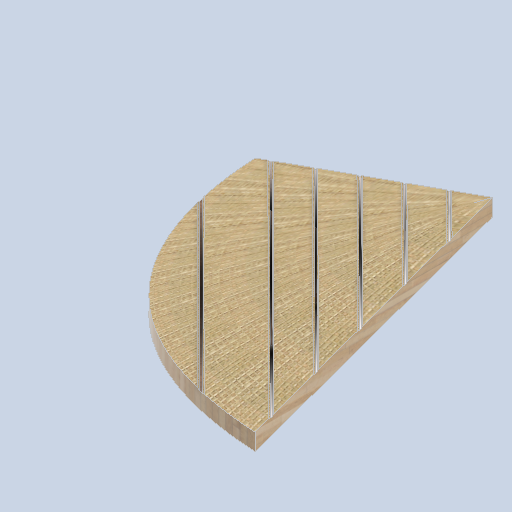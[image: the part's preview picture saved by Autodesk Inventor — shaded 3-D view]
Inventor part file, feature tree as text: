
AUTODESK INVENTOR PART (.ipt)
format: ipt  version: 2024.2 (Build 282272000, 272)  size: 927,744 bytes
history: native  units: in
note: dims shown in document units (in); Inventor stores cm internally (conversion verified against a paired STEP export)
features: sketch x19, plane x6, other x3
ambient origin geometry x8: Origin, YZ Plane, XZ Plane, XY Plane, X Axis, Y Axis, Z Axis, Center Point
bodies: Solid1 (feature_tree)
feature tree (28):
  other  "side_curve_corner_panel_MIR.ipt"
  other  "Solid1::side_curve_corner_panel_MIR.ipt"
  other  "TaggingFeature1"
  sketch  "Sketch1"  dims[d0=0.3937in]
  sketch  "Sketch2"
  sketch  "Sketch3"
  sketch  "Sketch4"
  sketch  "Sketch5"
  sketch  "Sketch6"
  sketch  "Sketch7"
  sketch  "Sketch8"
  sketch  "Sketch9"
  sketch  "Sketch10"
  sketch  "Sketch11"
  sketch  "Sketch12"
  sketch  "Sketch13"
  sketch  "Sketch14"
  sketch  "Sketch15"
  sketch  "Sketch16"
  sketch  "Sketch17"
  sketch  "Sketch18"
  sketch  "Sketch19"
  plane  "Work Plane1"
  plane  "Work Plane2"
  plane  "Work Plane3"
  plane  "Work Plane4"
  plane  "Work Plane5"
  plane  "Work Plane6"
